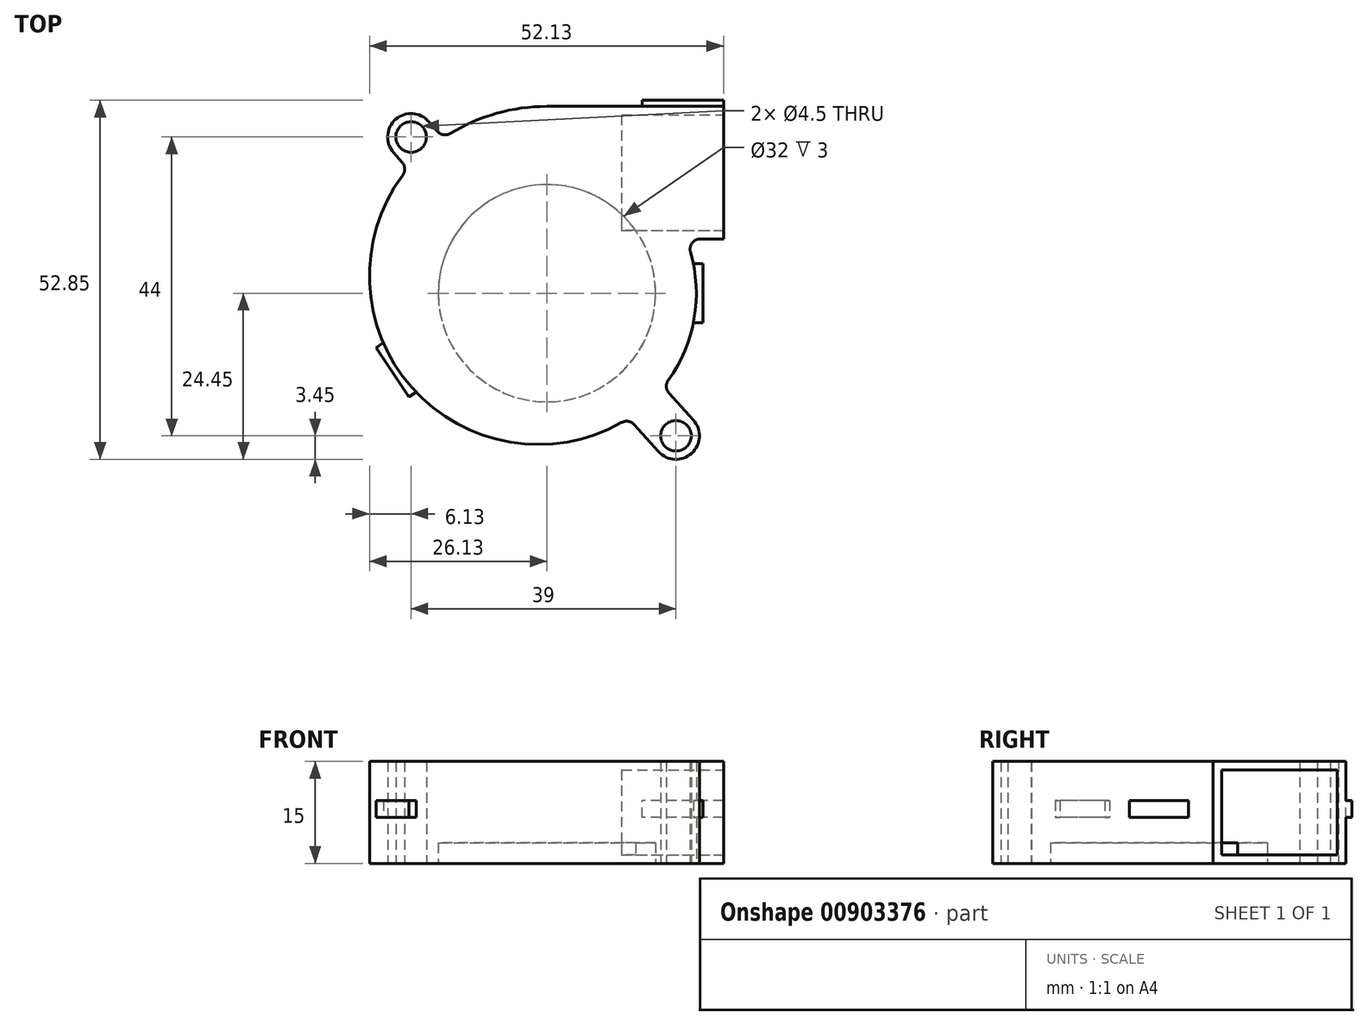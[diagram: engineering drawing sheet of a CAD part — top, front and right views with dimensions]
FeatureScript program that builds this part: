
annotation { "Feature Type Name" : "Feature", "Feature Type Description" : "" }
export const myFeature = defineFeature(function(context is Context, id is Id, definition is map)
    precondition{}
    {
        {
            var Q0;
            Q0=qCreatedBy(makeId("Top.planeOp"),FACE);
            var sketch = newSketch(context, id + "F0", { "sketchPlane" : qUnion([Q0])});
            skLineSegment(sketch, "E0", {"start": v(26, 27.5) * mm, "end": v(26, 8) * mm});
            skLineSegment(sketch, "E1", {"start": v(26, 8) * mm, "end": v(22.58, 8) * mm});
            skLineSegment(sketch, "E2", {"start": v(26, 27.5) * mm, "end": v(0, 27.5) * mm});
            skLineSegment(sketch, "E3", {"start": v(0, 0) * mm, "end": v(-23.77, 27.34) * mm, "construction": true});
            skLineSegment(sketch, "E4", {"start": v(0, 0) * mm, "end": v(-32.33, 0) * mm, "construction": true});
            skLineSegment(sketch, "E5", {"start": v(-16.15, 23.83) * mm, "end": v(-17.4, 25.26) * mm});
            skLineSegment(sketch, "E6", {"start": v(-21.32, 19.26) * mm, "end": v(-22.6, 20.74) * mm});
            skArc(sketch, "E7", {"start": v(-17.4, 25.26) * mm, "mid": v(-22.26, 25.6) * mm, "end": v(-22.6, 20.74) * mm});
            skCircle(sketch, "E8", {"center": v(-20, 23) * mm, "radius": 2.25 * mm});
            skArc(sketch, "E9", {"start": v(0, 27.5) * mm, "mid": v(-7.4, 26.49) * mm, "end": v(-14.24, 23.53) * mm});
            skLineSegment(sketch, "E10", {"start": v(0, 0) * mm, "end": v(12.38, 10.76) * mm, "construction": true});
            skLineSegment(sketch, "E11.MirrorCS", {"start": v(17.97, -14.72) * mm, "end": v(21.56, -18.69) * mm});
            skArc(sketch, "E12.MirrorCS", {"start": v(21.56, -18.69) * mm, "mid": v(21.31, -23.56) * mm, "end": v(16.44, -23.31) * mm});
            skLineSegment(sketch, "E13.MirrorCS", {"start": v(12.85, -19.34) * mm, "end": v(16.44, -23.31) * mm});
            skCircle(sketch, "E14.MirrorC", {"center": v(19, -21) * mm, "radius": 2.25 * mm});
            skLineSegment(sketch, "E15", {"start": v(0, 0) * mm, "end": v(0, -33.36) * mm, "construction": true});
            skLineSegment(sketch, "E16", {"start": v(0, 0) * mm, "end": v(19, -21) * mm, "construction": true});
            skArc(sketch, "E17", {"start": v(17.87, -12.84) * mm, "mid": v(21.68, -3.75) * mm, "end": v(21.14, 6.09) * mm});
            skPoint(sketch, "E18.visualSharp", {"position": v(-15.3, 22.85) * mm});
            skArc(sketch, "E18.filletArc", {"start": v(-16.15, 23.83) * mm, "mid": v(-15.25, 23.33) * mm, "end": v(-14.24, 23.53) * mm});
            skArc(sketch, "E19", {"start": v(-21.24, 17.38) * mm, "mid": v(-19.9, -13.9) * mm, "end": v(11, -19.04) * mm});
            skPoint(sketch, "E20", {"position": v(-26, 0) * mm});
            skPoint(sketch, "E21", {"position": v(22, 0) * mm});
            skPoint(sketch, "E22.visualSharp", {"position": v(-20.5, 18.32) * mm});
            skArc(sketch, "E22.filletArc", {"start": v(-21.24, 17.38) * mm, "mid": v(-20.95, 18.33) * mm, "end": v(-21.32, 19.26) * mm});
            skPoint(sketch, "E23.visualSharp", {"position": v(20.5, 8) * mm});
            skArc(sketch, "E23.filletArc", {"start": v(22.58, 8) * mm, "mid": v(21.38, 7.4) * mm, "end": v(21.14, 6.09) * mm});
            skPoint(sketch, "E24.visualSharp", {"position": v(17.14, -13.8) * mm});
            skArc(sketch, "E24.filletArc", {"start": v(17.87, -12.84) * mm, "mid": v(17.59, -13.8) * mm, "end": v(17.97, -14.72) * mm});
            skPoint(sketch, "E25.visualSharp", {"position": v(12.02, -18.43) * mm});
            skArc(sketch, "E25.filletArc", {"start": v(12.85, -19.34) * mm, "mid": v(11.97, -18.87) * mm, "end": v(11, -19.04) * mm});
            skSolve(sketch);
        }
        {
            var Q0;
            Q0 = qSketchRegion(id + "F0", true);
            extrude(context, id + "F1", {"entities" : qUnion([Q0]), "depth" : 7 * mm, "offsetDistance" : 25 * mm, "hasSecondDirection" : true, "secondDirectionOppositeDirection" : true, "secondDirectionDepth" : 8 * mm});
        }
        {
            var Q0;
            Q0=makeQuery(id+"F1.opExtrude","CAP_FACE",FACE,{"disambiguationData":[OSD([sQuery(id+"F0.wireOp",EDGE,"E0"),sQuery(id+"F0.wireOp",EDGE,"E1"),sQuery(id+"F0.wireOp",EDGE,"E2"),sQuery(id+"F0.wireOp",EDGE,"E5"),sQuery(id+"F0.wireOp",EDGE,"E6"),sQuery(id+"F0.wireOp",EDGE,"E7"),sQuery(id+"F0.wireOp",EDGE,"E8"),sQuery(id+"F0.wireOp",EDGE,"E9"),sQuery(id+"F0.wireOp",EDGE,"E11.MirrorCS"),sQuery(id+"F0.wireOp",EDGE,"E12.MirrorCS"),sQuery(id+"F0.wireOp",EDGE,"E13.MirrorCS"),sQuery(id+"F0.wireOp",EDGE,"E14.MirrorC"),sQuery(id+"F0.wireOp",EDGE,"E17"),sQuery(id+"F0.wireOp",EDGE,"E18.filletArc"),sQuery(id+"F0.wireOp",EDGE,"E19"),sQuery(id+"F0.wireOp",EDGE,"E22.filletArc"),sQuery(id+"F0.wireOp",EDGE,"E23.filletArc"),sQuery(id+"F0.wireOp",EDGE,"E24.filletArc"),sQuery(id+"F0.wireOp",EDGE,"E25.filletArc")])],"isStart":true});
            var sketch = newSketch(context, id + "F2", { "sketchPlane" : qUnion([Q0])});
            skCircle(sketch, "E26", {"center": v(0, 0) * mm, "radius": 16 * mm});
            skSolve(sketch);
        }
        {
            var Q0;
            Q0 = qSketchRegion(id + "F2", true);
            extrude(context, id + "F3", {"entities" : qUnion([Q0]), "operationType" : NewBodyOperationType.REMOVE, "oppositeDirection" : true, "depth" : 3 * mm, "offsetDistance" : 25 * mm});
        }
        {
            var Q0;
            Q0=qCreatedBy(makeId("Top.planeOp"),FACE);
            var sketch = newSketch(context, id + "F4", { "sketchPlane" : qUnion([Q0])});
            skLineSegment(sketch, "E27.bottom", {"start": v(26, 28.4) * mm, "end": v(14, 28.4) * mm});
            skLineSegment(sketch, "E27.top", {"start": v(26, 25.8) * mm, "end": v(14, 25.8) * mm});
            skLineSegment(sketch, "E27.left", {"start": v(26, 28.4) * mm, "end": v(26, 25.8) * mm});
            skLineSegment(sketch, "E27.right", {"start": v(14, 28.4) * mm, "end": v(14, 25.8) * mm});
            skLineSegment(sketch, "E28.bottom", {"start": v(23, 4.38) * mm, "end": v(20.84, 4.38) * mm});
            skLineSegment(sketch, "E28.top", {"start": v(23, -4.38) * mm, "end": v(20.84, -4.38) * mm});
            skLineSegment(sketch, "E28.left", {"start": v(23, 4.38) * mm, "end": v(23, -4.38) * mm});
            skLineSegment(sketch, "E28.right", {"start": v(20.84, 4.38) * mm, "end": v(20.84, -4.38) * mm});
            skLineSegment(sketch, "E29", {"start": v(-25.17, -8) * mm, "end": v(-20.34, -15.3) * mm});
            skLineSegment(sketch, "E30", {"start": v(-20.34, -15.3) * mm, "end": v(-17.7, -13.55) * mm});
            skLineSegment(sketch, "E31", {"start": v(-17.7, -13.55) * mm, "end": v(-22.53, -6.25) * mm});
            skLineSegment(sketch, "E32", {"start": v(-25.17, -8) * mm, "end": v(-22.53, -6.25) * mm});
            skLineSegment(sketch, "E33", {"start": v(0, 0) * mm, "end": v(26.85, 0) * mm, "construction": true});
            skPoint(sketch, "E34", {"position": v(23, 0) * mm});
            skPoint(sketch, "E35", {"position": v(22, 0) * mm});
            skPoint(sketch, "E36", {"position": v(-22, -11.15) * mm});
            skLineSegment(sketch, "E37", {"start": v(-20.3, -13.73) * mm, "end": v(-22, -11.15) * mm, "construction": true});
            skLineSegment(sketch, "E38", {"start": v(-22.75, -11.65) * mm, "end": v(-22, -11.15) * mm, "construction": true});
            skSolve(sketch);
        }
        {
            var Q0;
            Q0 = qSketchRegion(id + "F4", true);
            extrude(context, id + "F5", {"entities" : qUnion([Q0]), "operationType" : NewBodyOperationType.ADD, "endBound" : BoundingType.SYMMETRIC, "depth" : 2.5 * mm, "offsetDistance" : 25 * mm});
        }
        {
            var Q0;
            Q0=makeQuery(id+"F5.boolean.opBoolean","MERGE",FACE,{"derivedFrom":[makeQuery(id+"F1.opExtrude","SWEPT_FACE",FACE,{"disambiguationData":[OSD([sQuery(id+"F0.wireOp",EDGE,"E0")])]}),makeQuery(id+"F5.opExtrude","SWEPT_FACE",FACE,{"disambiguationData":[OSD([sQuery(id+"F4.wireOp",EDGE,"E27.left")])]})]});
            var sketch = newSketch(context, id + "F6", { "sketchPlane" : qUnion([Q0])});
            skLineSegment(sketch, "E39.0", {"start": v(26.25, 5.75) * mm, "end": v(26.25, -6.75) * mm});
            skLineSegment(sketch, "E39.1", {"start": v(26.25, 5.75) * mm, "end": v(9.25, 5.75) * mm});
            skLineSegment(sketch, "E39.2", {"start": v(9.25, 5.75) * mm, "end": v(9.25, -6.75) * mm});
            skLineSegment(sketch, "E39.3", {"start": v(26.25, -6.75) * mm, "end": v(9.25, -6.75) * mm});
            skSolve(sketch);
        }
        {
            var Q0;
            Q0 = qSketchRegion(id + "F6", true);
            extrude(context, id + "F7", {"entities" : qUnion([Q0]), "operationType" : NewBodyOperationType.REMOVE, "oppositeDirection" : true, "depth" : 15 * mm, "offsetDistance" : 25 * mm});
        }
    });
